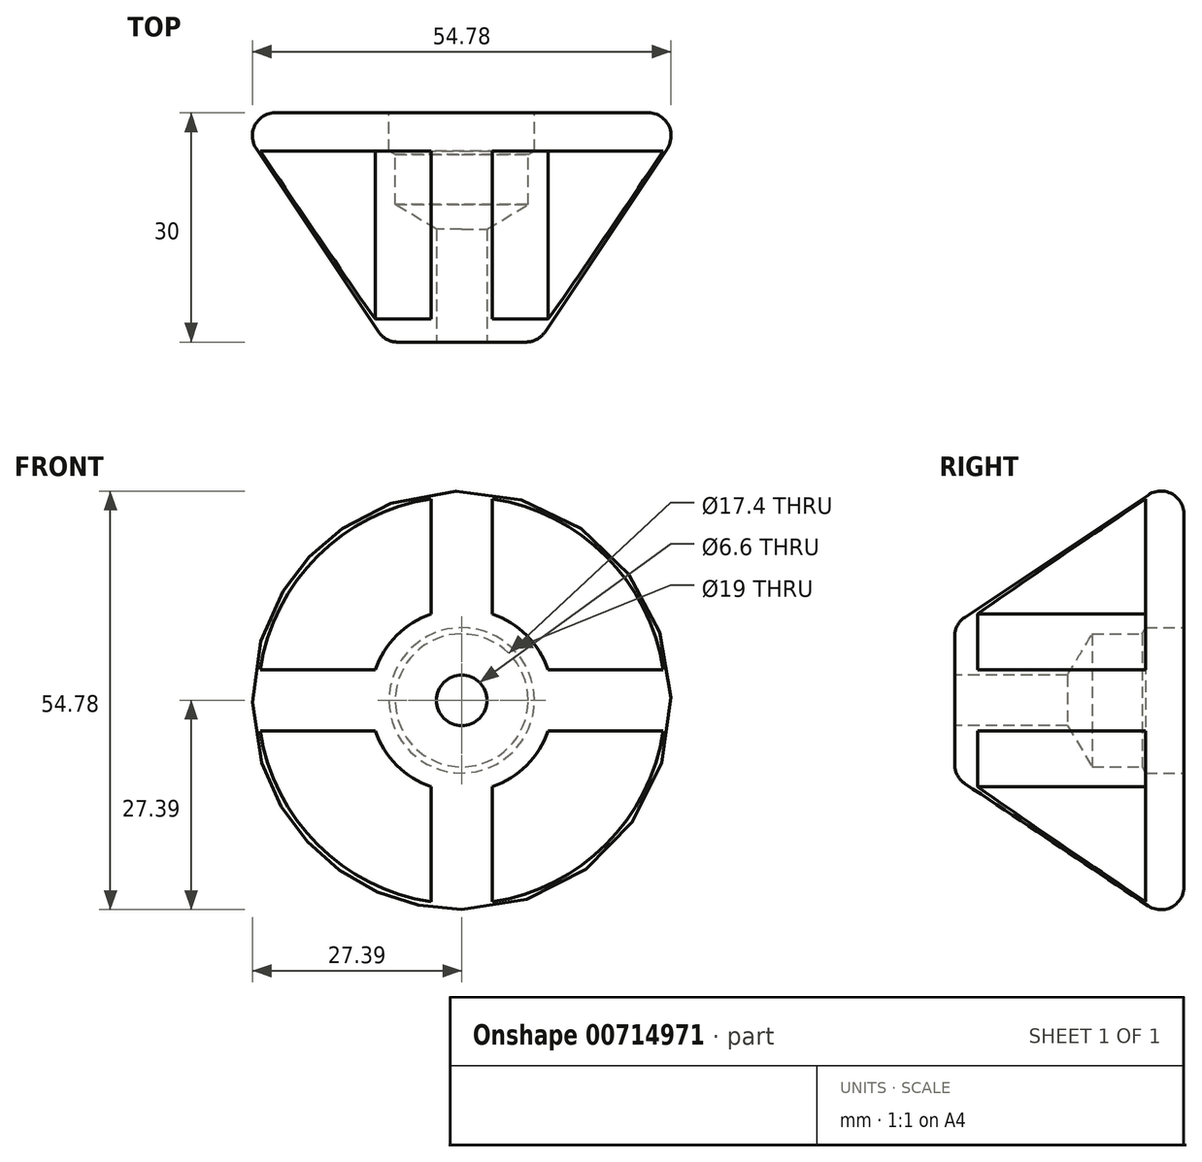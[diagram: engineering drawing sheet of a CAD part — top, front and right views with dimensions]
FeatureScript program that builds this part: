
annotation { "Feature Type Name" : "Feature", "Feature Type Description" : "" }
export const myFeature = defineFeature(function(context is Context, id is Id, definition is map)
    precondition{}
    {
        {
            var Q0;
            Q0=qCreatedBy(makeId("Right.planeOp"),FACE);
            var sketch = newSketch(context, id + "F0", { "sketchPlane" : qUnion([Q0])});
            skLineSegment(sketch, "E0", {"start": v(0, 0) * mm, "end": v(-30, 0) * mm});
            skLineSegment(sketch, "E1", {"start": v(-30, 0) * mm, "end": v(-30, 10) * mm});
            skLineSegment(sketch, "E2", {"start": v(-30, 10) * mm, "end": v(0, 30) * mm});
            skLineSegment(sketch, "E3", {"start": v(0, 30) * mm, "end": v(0, 0) * mm});
            skSolve(sketch);
        }
        {
            var Q0;
            Q0=makeQuery(id+"F0.imprint","IMPRINT",FACE,{"disambiguationData":[TD([[makeQuery(id+"F0.imprint","IMPRINT",EDGE,{"derivedFrom":sQuery(id+"F0.wireOp",EDGE,"E0")}),-1.0]])]});
            var Q1;
            Q1=sQuery(id+"F0.wireOp",EDGE,"E0");
            revolve(context, id + "F1", {"surfaceOperationType" : NewSurfaceOperationType.NEW, "entities" : qUnion([Q0]), "axis" : qUnion([Q1]), "revolveType" : RevolveType.FULL});
        }
        {
            var Q0;
            Q0=makeQuery(id+"F1.opRevolve","SWEPT_FACE",FACE,{"disambiguationData":[OSD([sQuery(id+"F0.wireOp",EDGE,"E1")])]});
            var sketch = newSketch(context, id + "F2", { "sketchPlane" : qUnion([Q0])});
            skArc(sketch, "E4", {"start": v(4, -11.31) * mm, "mid": v(8.49, -8.49) * mm, "end": v(11.31, -4) * mm});
            skArc(sketch, "E5", {"start": v(4, -27.31) * mm, "mid": v(19.52, -19.52) * mm, "end": v(27.31, -4) * mm});
            skLineSegment(sketch, "E6", {"start": v(27.31, -4) * mm, "end": v(11.31, -4) * mm});
            skLineSegment(sketch, "E7", {"start": v(4, -27.31) * mm, "end": v(4, -11.31) * mm});
            skLineSegment(sketch, "E8.1.0", {"start": v(27.31, 4) * mm, "end": v(11.31, 4) * mm});
            skLineSegment(sketch, "E8.1.1", {"start": v(4, 27.31) * mm, "end": v(4, 11.31) * mm});
            skArc(sketch, "E8.1.2", {"start": v(27.31, 4) * mm, "mid": v(19.52, 19.52) * mm, "end": v(4, 27.31) * mm});
            skArc(sketch, "E8.1.3", {"start": v(11.31, 4) * mm, "mid": v(8.49, 8.49) * mm, "end": v(4, 11.31) * mm});
            skLineSegment(sketch, "E8.2.0", {"start": v(-4, 27.31) * mm, "end": v(-4, 11.31) * mm});
            skLineSegment(sketch, "E8.2.1", {"start": v(-27.31, 4) * mm, "end": v(-11.31, 4) * mm});
            skArc(sketch, "E8.2.2", {"start": v(-4, 27.31) * mm, "mid": v(-19.52, 19.52) * mm, "end": v(-27.31, 4) * mm});
            skArc(sketch, "E8.2.3", {"start": v(-4, 11.31) * mm, "mid": v(-8.49, 8.49) * mm, "end": v(-11.31, 4) * mm});
            skLineSegment(sketch, "E8.3.0", {"start": v(-27.31, -4) * mm, "end": v(-11.31, -4) * mm});
            skLineSegment(sketch, "E8.3.1", {"start": v(-4, -27.31) * mm, "end": v(-4, -11.31) * mm});
            skArc(sketch, "E8.3.2", {"start": v(-27.31, -4) * mm, "mid": v(-19.52, -19.52) * mm, "end": v(-4, -27.31) * mm});
            skArc(sketch, "E8.3.3", {"start": v(-11.31, -4) * mm, "mid": v(-8.49, -8.49) * mm, "end": v(-4, -11.31) * mm});
            skSolve(sketch);
        }
        {
            var Q0;
            Q0=sQuery(id+"F2.wireOp",VERTEX,"E4.center");
            var Q1;
            Q1=makeQuery(id+"F1.opRevolve","SWEPT_BODY",BODY,{"disambiguationData":[OSD([sQuery(id+"F0.wireOp",EDGE,"E0"),sQuery(id+"F0.wireOp",EDGE,"E1"),sQuery(id+"F0.wireOp",EDGE,"E2"),sQuery(id+"F0.wireOp",EDGE,"E3")])]});
            hole(context, id + "F3", {"style" : HoleStyle.SIMPLE, "endStyle" : HoleEndStyle.THROUGH, "standardTappedOrClearance" : lookupTablePath({ "standard" : "ISO", "fit" : "Normal", "size" : "M6", "type" : "Clearance" }), "standardBlindInLast" : lookupTablePath({ "fit" : "Standard", "standard" : "ISO", "size" : "M6", "type" : "Clearance" }), "holeDiameter" : 6.6 * mm, "majorDiameter" : 5 * mm, "isTappedThrough" : true, "tappedDepth" : 12 * mm, "tapClearance" : 3, "locations" : qUnion([Q0]), "scope" : qUnion([Q1])});
        }
        {
            var Q0;
            Q0=makeQuery(id+"F1.opRevolve","SWEPT_FACE",FACE,{"disambiguationData":[OSD([sQuery(id+"F0.wireOp",EDGE,"E3")])]});
            var sketch = newSketch(context, id + "F4", { "sketchPlane" : qUnion([Q0])});
            skPoint(sketch, "E9", {"position": v(0, 0) * mm});
            skSolve(sketch);
        }
        {
            var Q0;
            Q0=sQuery(id+"F4.wireOp",VERTEX,"E9");
            var Q1;
            Q1=makeQuery(id+"F1.opRevolve","SWEPT_BODY",BODY,{"disambiguationData":[OSD([sQuery(id+"F0.wireOp",EDGE,"E0"),sQuery(id+"F0.wireOp",EDGE,"E1"),sQuery(id+"F0.wireOp",EDGE,"E2"),sQuery(id+"F0.wireOp",EDGE,"E3")])]});
            hole(context, id + "F5", {"style" : HoleStyle.SIMPLE, "endStyle" : HoleEndStyle.BLIND, "holeDiameter" : 17.4 * mm, "majorDiameter" : 5 * mm, "holeDepth" : 12 * mm, "isTappedThrough" : true, "tappedDepth" : 12 * mm, "tapClearance" : 3, "locations" : qUnion([Q0]), "scope" : qUnion([Q1])});
        }
        {
            var Q0;
            Q0=sQuery(id+"F4.wireOp",VERTEX,"E9");
            var Q1;
            Q1=makeQuery(id+"F1.opRevolve","SWEPT_BODY",BODY,{"disambiguationData":[OSD([sQuery(id+"F0.wireOp",EDGE,"E0"),sQuery(id+"F0.wireOp",EDGE,"E1"),sQuery(id+"F0.wireOp",EDGE,"E2"),sQuery(id+"F0.wireOp",EDGE,"E3")])]});
            hole(context, id + "F6", {"style" : HoleStyle.SIMPLE, "endStyle" : HoleEndStyle.BLIND, "holeDiameter" : 19 * mm, "majorDiameter" : 5 * mm, "holeDepth" : 5 * mm, "isTappedThrough" : true, "tappedDepth" : 12 * mm, "tapClearance" : 3, "locations" : qUnion([Q0]), "scope" : qUnion([Q1])});
        }
        {
            var Q0;
            Q0 = qSketchRegion(id + "F2", true);
            extrude(context, id + "F7", {"entities" : qUnion([Q0]), "operationType" : NewBodyOperationType.REMOVE, "oppositeDirection" : true, "depth" : 25 * mm, "offsetDistance" : 25 * mm});
        }
        {
            var Q0;
            Q0=makeQuery(id+"F1.opRevolve","SWEPT_EDGE",EDGE,{"disambiguationData":[OSD([sQuery(id+"F0.wireOp",EDGE,"E2"),sQuery(id+"F0.wireOp",EDGE,"E3")])]});
            var Q1;
            Q1=makeQuery(id+"F1.opRevolve","SWEPT_EDGE",EDGE,{"disambiguationData":[OSD([sQuery(id+"F0.wireOp",EDGE,"E1"),sQuery(id+"F0.wireOp",EDGE,"E2")])]});
            fillet(context, id + "F8", {"entities" : qUnion([Q0, Q1]), "radius" : 3 * mm, "tangentPropagation" : true, "allowEdgeOverflow" : false});
        }
    });
